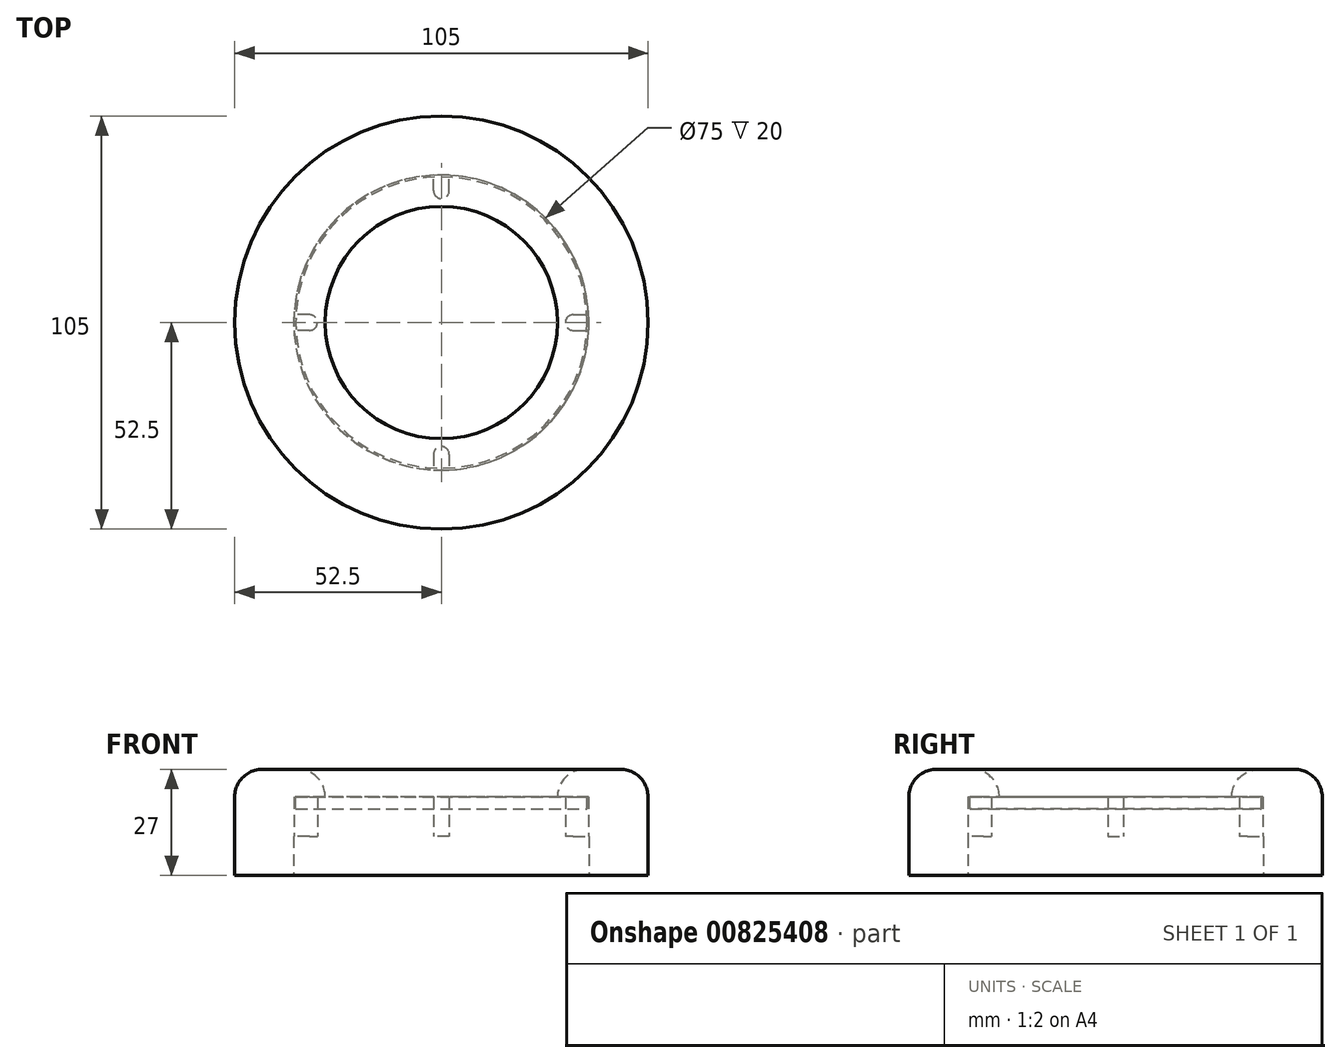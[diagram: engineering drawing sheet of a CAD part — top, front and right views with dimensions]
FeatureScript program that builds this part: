
annotation { "Feature Type Name" : "Feature", "Feature Type Description" : "" }
export const myFeature = defineFeature(function(context is Context, id is Id, definition is map)
    precondition{}
    {
        {
            var Q0;
            Q0=qCreatedBy(makeId("Top.planeOp"),FACE);
            var sketch = newSketch(context, id + "F0", { "sketchPlane" : qUnion([Q0])});
            skCircle(sketch, "E0", {"center": v(0, 0) * mm, "radius": 37.5 * mm});
            skCircle(sketch, "E1.0", {"center": v(0, 0) * mm, "radius": 52.5 * mm});
            skCircle(sketch, "E2.0", {"center": v(0, 0) * mm, "radius": 29.5 * mm});
            skPoint(sketch, "E3", {"position": v(0, 33.5) * mm});
            skPoint(sketch, "E4", {"position": v(0, -33.5) * mm});
            skPoint(sketch, "E5", {"position": v(-33.5, 0) * mm});
            skPoint(sketch, "E6", {"position": v(33.5, 0) * mm});
            skCircle(sketch, "E7", {"center": v(0, -33.5) * mm, "radius": 2 * mm});
            skCircle(sketch, "E8", {"center": v(33.5, 0) * mm, "radius": 2 * mm});
            skCircle(sketch, "E9", {"center": v(0, 33.5) * mm, "radius": 2 * mm});
            skCircle(sketch, "E10", {"center": v(-33.5, 0) * mm, "radius": 2 * mm});
            skLineSegment(sketch, "E11", {"start": v(-2, -33.5) * mm, "end": v(-2, -37.45) * mm});
            skLineSegment(sketch, "E12", {"start": v(2, -33.5) * mm, "end": v(2, -37.45) * mm});
            skLineSegment(sketch, "E13", {"start": v(-33.5, -2) * mm, "end": v(-37.45, -2) * mm});
            skLineSegment(sketch, "E14", {"start": v(-33.5, 2) * mm, "end": v(-37.45, 2) * mm});
            skLineSegment(sketch, "E15", {"start": v(33.5, -2) * mm, "end": v(37.45, -2) * mm});
            skLineSegment(sketch, "E16", {"start": v(33.5, 2) * mm, "end": v(37.45, 2) * mm});
            skLineSegment(sketch, "E17", {"start": v(-2, 33.5) * mm, "end": v(-2, 37.45) * mm});
            skLineSegment(sketch, "E18", {"start": v(2, 33.5) * mm, "end": v(2, 37.45) * mm});
            skSolve(sketch);
        }
        {
            var Q0;
            Q0=makeQuery(id+"F0.imprint","IMPRINT",FACE,{"disambiguationData":[TD([[makeQuery(id+"F0.imprint","IMPRINT",EDGE,{"derivedFrom":sQuery(id+"F0.wireOp",EDGE,"E0")}),-1.0]])]});
            var Q1;
            Q1=makeQuery(id+"F0.imprint","IMPRINT",FACE,{"disambiguationData":[TD([[makeQuery(id+"F0.imprint","IMPRINT",EDGE,{"derivedFrom":sQuery(id+"F0.wireOp",EDGE,"E0")}),1.0]])]});
            var Q2;
            Q2=makeQuery(id+"F0.imprint","IMPRINT",FACE,{"disambiguationData":[TD([[makeQuery(id+"F0.imprint","IMPRINT",EDGE,{"derivedFrom":sQuery(id+"F0.wireOp",EDGE,"E10")}),1.0]])]});
            var Q3;
            Q3=makeQuery(id+"F0.imprint","IMPRINT",FACE,{"disambiguationData":[TD([[makeQuery(id+"F0.imprint","IMPRINT",EDGE,{"derivedFrom":sQuery(id+"F0.wireOp",EDGE,"E7")}),1.0]])]});
            var Q4;
            Q4=makeQuery(id+"F0.imprint","IMPRINT",FACE,{"disambiguationData":[TD([[makeQuery(id+"F0.imprint","IMPRINT",EDGE,{"derivedFrom":sQuery(id+"F0.wireOp",EDGE,"E8")}),1.0]])]});
            var Q5;
            Q5=makeQuery(id+"F0.imprint","IMPRINT",FACE,{"disambiguationData":[TD([[makeQuery(id+"F0.imprint","IMPRINT",EDGE,{"derivedFrom":sQuery(id+"F0.wireOp",EDGE,"E9")}),1.0]])]});
            var Q6;
            {var subQ0=sQuery(id+"F0.wireOp",EDGE,"E13");Q6=makeQuery(id+"F0.imprint","IMPRINT",FACE,{"disambiguationData":[TD([[makeQuery(id+"F0.imprint","IMPRINT",EDGE,{"derivedFrom":subQ0}),-1.0]])]});}
            var Q7;
            {var subQ0=sQuery(id+"F0.wireOp",EDGE,"E11");Q7=makeQuery(id+"F0.imprint","IMPRINT",FACE,{"disambiguationData":[TD([[makeQuery(id+"F0.imprint","IMPRINT",EDGE,{"derivedFrom":subQ0}),1.0]])]});}
            var Q8;
            {var subQ0=sQuery(id+"F0.wireOp",EDGE,"Yl6inYzF-dnDD-AZqz-S6KJ-a1kRHPTBPkI2");Q8=makeQuery(id+"F0.imprint","IMPRINT",FACE,{"disambiguationData":[TD([[makeQuery(id+"F0.imprint","IMPRINT",EDGE,{"derivedFrom":subQ0}),-1.0]])]});}
            var Q9;
            {var subQ0=sQuery(id+"F0.wireOp",EDGE,"4wbEEJPF-ZOch-pFms-XabN-NiZQrBbR2OPV");Q9=makeQuery(id+"F0.imprint","IMPRINT",FACE,{"disambiguationData":[TD([[makeQuery(id+"F0.imprint","IMPRINT",EDGE,{"derivedFrom":subQ0}),1.0]])]});}
            var Q10;
            {var subQ0=sQuery(id+"F0.wireOp",EDGE,"E15");Q10=makeQuery(id+"F0.imprint","IMPRINT",FACE,{"disambiguationData":[TD([[makeQuery(id+"F0.imprint","IMPRINT",EDGE,{"derivedFrom":subQ0}),1.0]])]});}
            var Q11;
            {var subQ0=sQuery(id+"F0.wireOp",EDGE,"E17");Q11=makeQuery(id+"F0.imprint","IMPRINT",FACE,{"disambiguationData":[TD([[makeQuery(id+"F0.imprint","IMPRINT",EDGE,{"derivedFrom":subQ0}),-1.0]])]});}
            extrude(context, id + "F1", {"entities" : qUnion([Q0, Q1, Q2, Q3, Q4, Q5, Q6, Q7, Q8, Q9, Q10, Q11]), "depth" : 27 * mm, "offsetDistance" : 25 * mm});
        }
        {
            var Q0;
            Q0=makeQuery(id+"F0.imprint","IMPRINT",FACE,{"disambiguationData":[TD([[makeQuery(id+"F0.imprint","IMPRINT",EDGE,{"derivedFrom":sQuery(id+"F0.wireOp",EDGE,"E0")}),1.0]])]});
            extrude(context, id + "F2", {"entities" : qUnion([Q0]), "operationType" : NewBodyOperationType.REMOVE, "depth" : 20 * mm, "offsetDistance" : 25 * mm});
        }
        {
            var Q0;
            {var subQ0=sQuery(id+"F0.wireOp",EDGE,"E10");var subQ1=makeQuery(id+"F0.imprint","INTERSECT",VERTEX,{"derivedFrom":[subQ0,sQuery(id+"F0.wireOp",EDGE,"E13")]});Q0=makeQuery(id+"F0.imprint","IMPRINT",FACE,{"disambiguationData":[TD([[makeQuery(id+"F0.imprint","IMPRINT",EDGE,{"disambiguationData":[TD([[subQ1,1.0]])],"derivedFrom":subQ0}),1.0]])]});}
            var Q1;
            {var subQ0=sQuery(id+"F0.wireOp",EDGE,"E13");Q1=makeQuery(id+"F0.imprint","IMPRINT",FACE,{"disambiguationData":[TD([[makeQuery(id+"F0.imprint","IMPRINT",EDGE,{"derivedFrom":subQ0}),-1.0]])]});}
            var Q2;
            {var subQ0=sQuery(id+"F0.wireOp",EDGE,"E11");Q2=makeQuery(id+"F0.imprint","IMPRINT",FACE,{"disambiguationData":[TD([[makeQuery(id+"F0.imprint","IMPRINT",EDGE,{"derivedFrom":subQ0}),1.0]])]});}
            var Q3;
            {var subQ0=sQuery(id+"F0.wireOp",EDGE,"E7");var subQ1=makeQuery(id+"F0.imprint","INTERSECT",VERTEX,{"derivedFrom":[subQ0,sQuery(id+"F0.wireOp",EDGE,"E11")]});Q3=makeQuery(id+"F0.imprint","IMPRINT",FACE,{"disambiguationData":[TD([[makeQuery(id+"F0.imprint","IMPRINT",EDGE,{"disambiguationData":[TD([[subQ1,1.0]])],"derivedFrom":subQ0}),1.0]])]});}
            var Q4;
            {var subQ0=sQuery(id+"F0.wireOp",EDGE,"E15");Q4=makeQuery(id+"F0.imprint","IMPRINT",FACE,{"disambiguationData":[TD([[makeQuery(id+"F0.imprint","IMPRINT",EDGE,{"derivedFrom":subQ0}),1.0]])]});}
            var Q5;
            {var subQ0=sQuery(id+"F0.wireOp",EDGE,"E8");var subQ1=makeQuery(id+"F0.imprint","INTERSECT",VERTEX,{"derivedFrom":[subQ0,sQuery(id+"F0.wireOp",EDGE,"E15")]});Q5=makeQuery(id+"F0.imprint","IMPRINT",FACE,{"disambiguationData":[TD([[makeQuery(id+"F0.imprint","IMPRINT",EDGE,{"disambiguationData":[TD([[subQ1,1.0]])],"derivedFrom":subQ0}),1.0]])]});}
            var Q6;
            {var subQ0=sQuery(id+"F0.wireOp",EDGE,"E17");Q6=makeQuery(id+"F0.imprint","IMPRINT",FACE,{"disambiguationData":[TD([[makeQuery(id+"F0.imprint","IMPRINT",EDGE,{"derivedFrom":subQ0}),-1.0]])]});}
            var Q7;
            {var subQ0=sQuery(id+"F0.wireOp",EDGE,"E9");var subQ1=makeQuery(id+"F0.imprint","INTERSECT",VERTEX,{"derivedFrom":[subQ0,sQuery(id+"F0.wireOp",EDGE,"E17")]});Q7=makeQuery(id+"F0.imprint","IMPRINT",FACE,{"disambiguationData":[TD([[makeQuery(id+"F0.imprint","IMPRINT",EDGE,{"disambiguationData":[TD([[subQ1,1.0]])],"derivedFrom":subQ0}),1.0]])]});}
            extrude(context, id + "F3", {"entities" : qUnion([Q0, Q1, Q2, Q3, Q4, Q5, Q6, Q7]), "operationType" : NewBodyOperationType.REMOVE, "depth" : 10 * mm, "offsetDistance" : 25 * mm});
        }
        {
            var Q0;
            Q0=makeQuery(id+"F2.boolean.opBoolean","COPY",FACE,{"derivedFrom":makeQuery(id+"F2.opExtrude","CAP_FACE",FACE,{"disambiguationData":[OSD([sQuery(id+"F0.wireOp",EDGE,"E0"),sQuery(id+"F0.wireOp",EDGE,"E2.0"),sQuery(id+"F0.wireOp",EDGE,"E7"),sQuery(id+"F0.wireOp",EDGE,"E8"),sQuery(id+"F0.wireOp",EDGE,"E9"),sQuery(id+"F0.wireOp",EDGE,"E10"),sQuery(id+"F0.wireOp",EDGE,"E11"),sQuery(id+"F0.wireOp",EDGE,"E12"),sQuery(id+"F0.wireOp",EDGE,"E13"),sQuery(id+"F0.wireOp",EDGE,"E14"),sQuery(id+"F0.wireOp",EDGE,"E15"),sQuery(id+"F0.wireOp",EDGE,"E16"),sQuery(id+"F0.wireOp",EDGE,"E17"),sQuery(id+"F0.wireOp",EDGE,"E18")])],"isStart":false})});
            var sketch = newSketch(context, id + "F4", { "sketchPlane" : qUnion([Q0])});
            skCircle(sketch, "E19", {"center": v(0, 0) * mm, "radius": 37 * mm});
            skSolve(sketch);
        }
        {
            var Q0;
            Q0 = qSketchRegion(id + "F4", true);
            var Q1;
            Q1=makeQuery(id+"F4.imprint","IMPRINT",FACE,{"disambiguationData":[TD([[makeQuery(id+"F4.imprint","IMPRINT",EDGE,{"derivedFrom":makeQuery(id+"F2.boolean.opBoolean","COPY",EDGE,{"derivedFrom":makeQuery(id+"F2.opExtrude","CAP_EDGE",EDGE,{"disambiguationData":[OSD([sQuery(id+"F0.wireOp",EDGE,"E2.0")])],"isStart":false})})}),-1.0]])]});
            extrude(context, id + "F5", {"entities" : qUnion([Q0, Q1]), "depth" : 3 * mm, "offsetDistance" : 25 * mm});
        }
        {
            var Q0;
            Q0=makeQuery(id+"F1.opExtrude","CAP_EDGE",EDGE,{"disambiguationData":[OSD([sQuery(id+"F0.wireOp",EDGE,"E1.0")])],"isStart":false});
            var Q1;
            Q1=makeQuery(id+"F1.opExtrude","CAP_EDGE",EDGE,{"disambiguationData":[OSD([sQuery(id+"F0.wireOp",EDGE,"E2.0")])],"isStart":false});
            fillet(context, id + "F6", {"entities" : qUnion([Q0, Q1]), "radius" : 7 * mm, "tangentPropagation" : true, "allowEdgeOverflow" : false});
        }
    });
